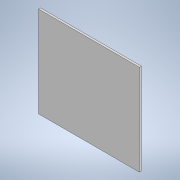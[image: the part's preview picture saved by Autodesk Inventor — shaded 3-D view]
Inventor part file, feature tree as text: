
AUTODESK INVENTOR PART (.ipt)
format: ipt  version: 2020.2 (Build 242310000, 310)  size: 89,600 bytes
history: native  units: mm
features: extrude x1, sketch x1
ambient origin geometry x8: Origin, YZ Plane, XZ Plane, XY Plane, X Axis, Y Axis, Z Axis, Center Point
bodies: Solid1 (feature_tree)
feature tree (2):
  extrude  "Extrusion1"  Depth=90.0mm
  sketch  "Sketch1"  dims[d0=100.0mm d1=90.0mm d2=2.0mm d3=0.0mm]
